# Revit family: Haworth_MSeries_Storage_Pedestal_AP_PRELIMINARY
name_source: partatom
category: Furniture Systems
units: mm (PartAtom-declared; Revit-internal decimal feet)

## family parameters
Always vertical = Yes
Cut with Voids When Loaded = No
OmniClass Number = 23.40.70.14.64.21
OmniClass Title = Systems Furniture
Part Type = Normal
Room Calculation Point = No
Round Connector Dimension = Use Diameter
Shared = No
Work Plane-Based = No

## types (4) — shared parameters
3 Drawer Control = Yes
Assembly Code = E2020200
Box Box File = Yes
Box File = No
Case Thickness = 19 mm  [stored 0.062336 ft]
Caster Back Offset = 30 mm  [stored 0.0984252 ft]
Caster Finish = Haworth _ Polymer _ Black
Caster Front Offset = 48 mm  [stored 0.15748 ft]
Casters Side Offset = 40 mm  [stored 0.131234 ft]
Custom Size = No
Description = Haworth - M Series - Storage - Pedestal
Distance Between Drawer = 6 mm  [stored 0.019685 ft]
Glide Finish = Haworth _ Polymer _ Black
Inner Drawer = Haworth _ Polymer _ Black
Linear Pull Length = 200 mm  [stored 0.656168 ft]
Manufacturer = Haworth
Max. Depth = 525 mm
Max. Height = 695 mm  [stored 2.28018 ft]
Max. Width = 395 mm  [stored 1.29593 ft]
Min. Height = 503 mm  [stored 1.65026 ft]
Min. Width = 300 mm
Model = STMSPXXN
Premise Pull Length = 4 mm  [stored 0.0131234 ft]
Pull Finish = Haworth _ Paint _ Smooth Plaster
Revision Number = 1
Side Case Back Control = 19 mm  [stored 0.062336 ft]
Size = Verify Final Dim. w/ Haworth
Small = No
Top Thickness = 19 mm  [stored 0.062336 ft]
Trim Finish = Haworth _ Polymer _ Black
URL = https://www.haworth.com
URL - Product = https://www.haworth.com
Warranty = http://www.haworth.com
With Lock = Yes
zero-valued in all types: Back Case Back Control, Back Case Side Control, Top Case Back Control

## per-type parameters (varying)
| type | Actual Depth | Actual Height | Actual Width | Attached | Bottom Case Offset | Bottom Drawer Height | Bottom Drawer Offset | Cushion Height | Depth | Drawer Width | Glide Control | Large | Medium | Middle Drawer Height | Min. Depth | Mobile | Normal Style | Slim Style | Standard Storage Height | Top Drawer Height | Total Drawer Height |
| 503h 395w 525d | 520 mm  [stored 1.70604 ft] | 600 mm | 300 mm | No | 45 mm  [stored 0.147638 ft] | 262 mm  [stored 0.85958 ft] | 67 mm | 0 mm  [stored 0 ft] | 520 mm  [stored 1.70604 ft] | 297 mm | No | No | Yes | 131 mm  [stored 0.42979 ft] | 520 mm  [stored 1.70604 ft] | Yes | No | Yes | 600 mm | 131 mm  [stored 0.42979 ft] | 530 mm  [stored 1.73885 ft] |
| 600h 395w 525d | 525 mm | 600 mm | 395 mm  [stored 1.29593 ft] | No | 45 mm  [stored 0.147638 ft] | 262 mm  [stored 0.85958 ft] | 67 mm | 0 mm  [stored 0 ft] | 525 mm | 392 mm  [stored 1.28609 ft] | No | No | Yes | 131 mm  [stored 0.42979 ft] | 525 mm | Yes | Yes | No | 600 mm | 131 mm  [stored 0.42979 ft] | 530 mm  [stored 1.73885 ft] |
| 695h 395w 525d | 525 mm | 695 mm  [stored 2.28018 ft] | 395 mm  [stored 1.29593 ft] | Yes | 40 mm  [stored 0.131234 ft] | 312 mm  [stored 1.02362 ft] | 62 mm  [stored 0.203412 ft] | 10 mm  [stored 0.0328084 ft] | 525 mm | 392 mm  [stored 1.28609 ft] | Yes | Yes | No | 156 mm  [stored 0.511811 ft] | 525 mm | No | Yes | No | 695 mm  [stored 2.28018 ft] | 156 mm  [stored 0.511811 ft] | 630 mm  [stored 2.06693 ft] |
| 600h 300w 520d | 520 mm  [stored 1.70604 ft] | 600 mm | 300 mm | No | 45 mm  [stored 0.147638 ft] | 262 mm  [stored 0.85958 ft] | 67 mm | 0 mm  [stored 0 ft] | 520 mm  [stored 1.70604 ft] | 297 mm | No | No | Yes | 131 mm  [stored 0.42979 ft] | 520 mm  [stored 1.70604 ft] | Yes | No | Yes | 600 mm | 131 mm  [stored 0.42979 ft] | 530 mm  [stored 1.73885 ft] |

note: [stored X ft] marks values corroborated as IEEE doubles in the binary element streams (Revit-internal decimal feet)

## geometry (parser evidence)
native form markers: Sweep x24
no freeform markers — native parametric forms only
